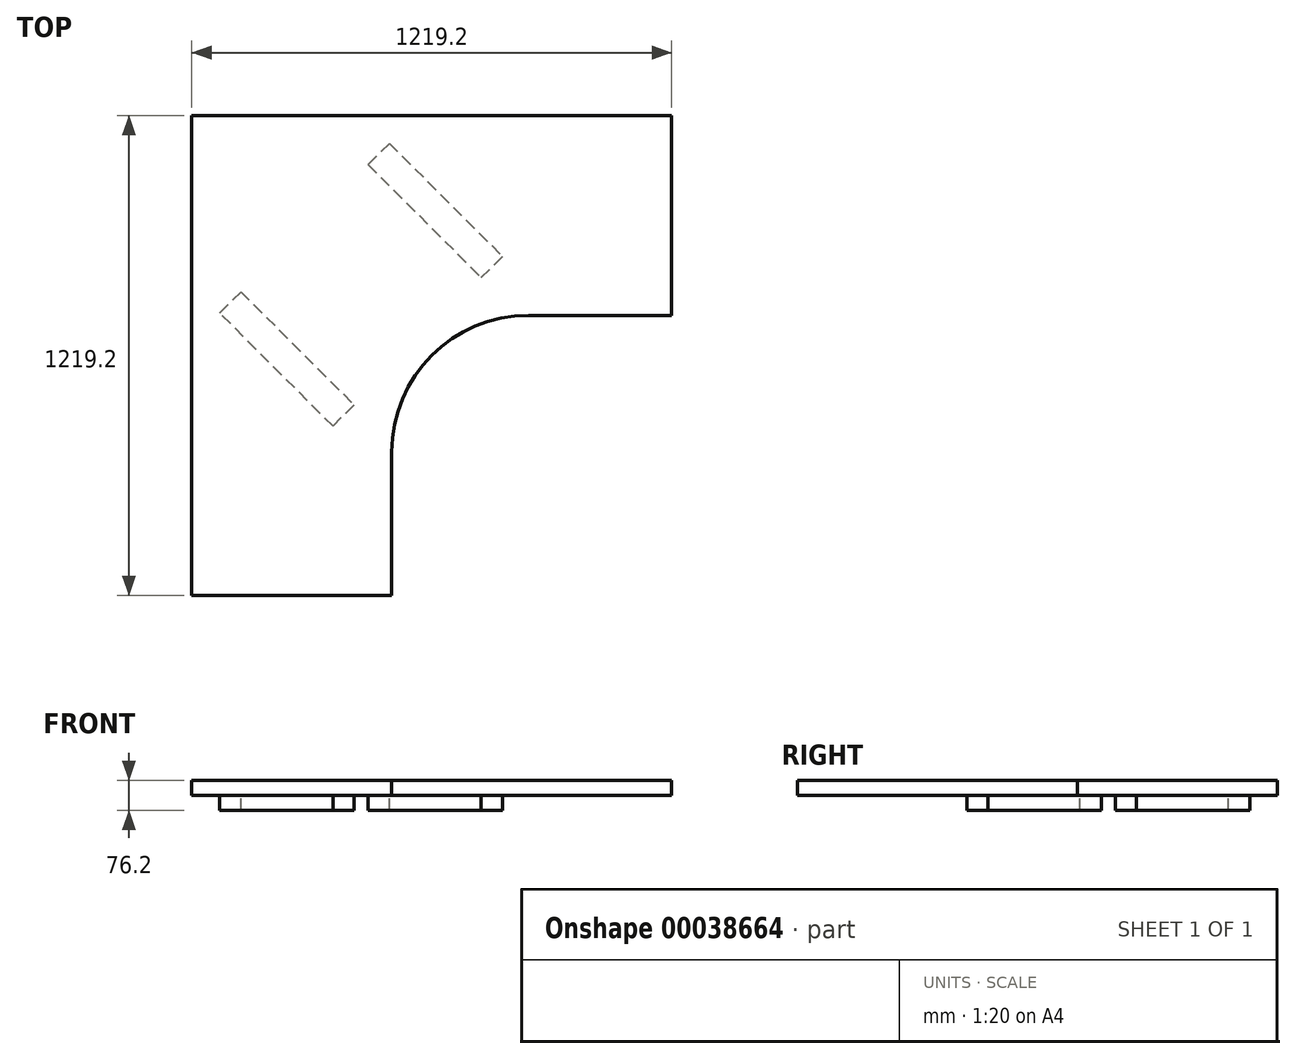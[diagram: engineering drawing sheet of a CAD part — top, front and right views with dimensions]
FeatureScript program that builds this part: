
annotation { "Feature Type Name" : "Feature", "Feature Type Description" : "" }
export const myFeature = defineFeature(function(context is Context, id is Id, definition is map)
    precondition{}
    {
        {
            var Q0;
            Q0=qCreatedBy(makeId("Top.planeOp"),FACE);
            var sketch = newSketch(context, id + "F0", { "sketchPlane" : qUnion([Q0])});
            skLineSegment(sketch, "E0.rect.bottom", {"start": v(609.6, 609.6) * mm, "end": v(-609.6, 609.6) * mm});
            skLineSegment(sketch, "E0.rect.top", {"start": v(-101.6, -609.6) * mm, "end": v(-609.6, -609.6) * mm});
            skLineSegment(sketch, "E0.rect.left", {"start": v(609.6, 609.6) * mm, "end": v(609.6, 101.6) * mm});
            skLineSegment(sketch, "E0.rect.right", {"start": v(-609.6, 609.6) * mm, "end": v(-609.6, -609.6) * mm});
            skPoint(sketch, "E0.rect.middle", {"position": v(0, 0) * mm});
            skArc(sketch, "E1", {"start": v(245.28, 101.6) * mm, "mid": v(0, 0) * mm, "end": v(-101.6, -245.28) * mm});
            skLineSegment(sketch, "E2", {"start": v(-101.6, -245.28) * mm, "end": v(-101.6, -609.6) * mm});
            skLineSegment(sketch, "E3", {"start": v(245.28, 101.6) * mm, "end": v(609.6, 101.6) * mm});
            skPoint(sketch, "E4.orphan", {"position": v(609.6, -609.6) * mm});
            skSolve(sketch);
        }
        {
            var Q0;
            Q0 = qSketchRegion(id + "F0", true);
            extrude(context, id + "F1", {"entities" : qUnion([Q0]), "depth" : 38.1 * mm});
        }
        {
            var Q0;
            Q0=makeQuery(id+"F1.opExtrude","CAP_FACE",FACE,{"disambiguationData":[OSD([sQuery(id+"F0.wireOp",EDGE,"E0.rect.bottom"),sQuery(id+"F0.wireOp",EDGE,"E0.rect.top"),sQuery(id+"F0.wireOp",EDGE,"E0.rect.left"),sQuery(id+"F0.wireOp",EDGE,"E0.rect.right"),sQuery(id+"F0.wireOp",EDGE,"E1"),sQuery(id+"F0.wireOp",EDGE,"E2"),sQuery(id+"F0.wireOp",EDGE,"E3")])],"isStart":true});
            var sketch = newSketch(context, id + "F2", { "sketchPlane" : qUnion([Q0])});
            skLineSegment(sketch, "E5", {"start": v(-251.45, 179.6) * mm, "end": v(-538.82, -107.76) * mm});
            skLineSegment(sketch, "E6", {"start": v(-538.82, -107.76) * mm, "end": v(-107.76, -538.82) * mm, "construction": true});
            skLineSegment(sketch, "E7", {"start": v(-107.76, -538.82) * mm, "end": v(179.6, -251.45) * mm});
            skLineSegment(sketch, "E8", {"start": v(179.6, -251.45) * mm, "end": v(-251.45, 179.6) * mm, "construction": true});
            skLineSegment(sketch, "E9", {"start": v(-609.6, -609.6) * mm, "end": v(0, 0) * mm, "construction": true});
            skPoint(sketch, "E10", {"position": v(-35.92, -35.92) * mm});
            skPoint(sketch, "E11", {"position": v(-323.29, -323.29) * mm});
            skLineSegment(sketch, "E12", {"start": v(-395.13, 35.92) * mm, "end": v(35.92, -395.13) * mm, "construction": true});
            skLineSegment(sketch, "E13", {"start": v(-538.82, -107.76) * mm, "end": v(-484.93, -161.64) * mm});
            skLineSegment(sketch, "E14", {"start": v(-484.93, -161.64) * mm, "end": v(-197.57, 125.72) * mm});
            skLineSegment(sketch, "E15", {"start": v(-197.57, 125.72) * mm, "end": v(-251.45, 179.6) * mm});
            skLineSegment(sketch, "E16.MirrorCS", {"start": v(-107.76, -538.82) * mm, "end": v(-161.64, -484.93) * mm});
            skLineSegment(sketch, "E17.MirrorCS", {"start": v(125.72, -197.57) * mm, "end": v(179.6, -251.45) * mm});
            skLineSegment(sketch, "E18.MirrorCS", {"start": v(-161.64, -484.93) * mm, "end": v(125.72, -197.57) * mm});
            skSolve(sketch);
        }
        {
            var Q0;
            Q0 = qSketchRegion(id + "F2", true);
            extrude(context, id + "F3", {"entities" : qUnion([Q0]), "operationType" : NewBodyOperationType.ADD, "depth" : 38.1 * mm});
        }
    });
